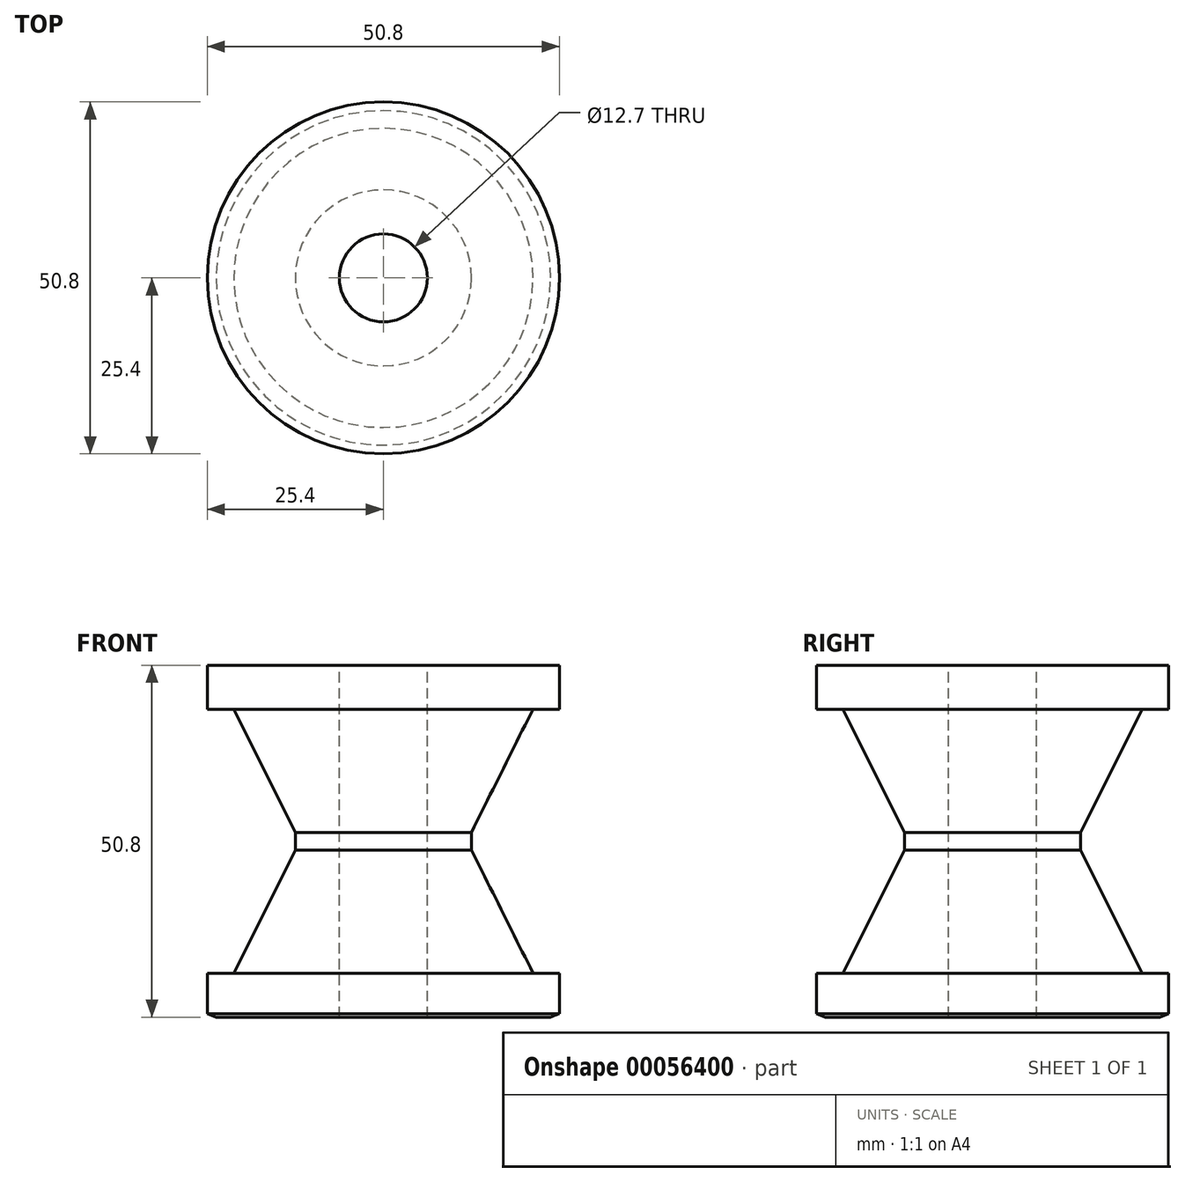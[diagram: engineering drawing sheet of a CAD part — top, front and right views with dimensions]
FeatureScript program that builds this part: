
annotation { "Feature Type Name" : "Feature", "Feature Type Description" : "" }
export const myFeature = defineFeature(function(context is Context, id is Id, definition is map)
    precondition{}
    {
        {
            var Q0;
            Q0=qCreatedBy(makeId("Front.planeOp"),FACE);
            var sketch = newSketch(context, id + "F0", { "sketchPlane" : qUnion([Q0])});
            skLineSegment(sketch, "E0.bottom", {"start": v(-12.7, 15.41) * mm, "end": v(-6.35, 15.41) * mm});
            skLineSegment(sketch, "E0.top", {"start": v(-12.7, -31.46) * mm, "end": v(-6.35, -31.46) * mm});
            skLineSegment(sketch, "E0.left", {"start": v(-12.7, 15.41) * mm, "end": v(-12.7, -31.46) * mm});
            skLineSegment(sketch, "E0.right", {"start": v(-6.35, 15.41) * mm, "end": v(-6.35, -31.46) * mm});
            skLineSegment(sketch, "E1.bottom", {"start": v(-6.35, 15.41) * mm, "end": v(-25.4, 15.41) * mm});
            skLineSegment(sketch, "E1.top", {"start": v(-6.35, 13) * mm, "end": v(-25.4, 13) * mm});
            skLineSegment(sketch, "E1.left", {"start": v(-6.35, 15.41) * mm, "end": v(-6.35, 13) * mm});
            skLineSegment(sketch, "E1.right", {"start": v(-25.4, 15.41) * mm, "end": v(-25.4, 13) * mm});
            skLineSegment(sketch, "E2.bottom", {"start": v(-6.35, -31.46) * mm, "end": v(-25.4, -31.46) * mm});
            skLineSegment(sketch, "E2.top", {"start": v(-6.35, -25.1) * mm, "end": v(-25.4, -25.1) * mm});
            skLineSegment(sketch, "E2.left", {"start": v(-6.35, -31.46) * mm, "end": v(-6.35, -25.1) * mm});
            skLineSegment(sketch, "E2.right", {"start": v(-25.4, -31.46) * mm, "end": v(-25.4, -25.1) * mm});
            skLineSegment(sketch, "E3.top", {"start": v(-6.35, 19.34) * mm, "end": v(-25.4, 19.34) * mm});
            skLineSegment(sketch, "E3.left", {"start": v(-6.35, 15.41) * mm, "end": v(-6.35, 19.34) * mm});
            skLineSegment(sketch, "E3.right", {"start": v(-25.4, 15.41) * mm, "end": v(-25.4, 19.34) * mm});
            skLineSegment(sketch, "E4", {"start": v(-31.56, 0) * mm, "end": v(32.14, 0) * mm, "construction": true});
            skLineSegment(sketch, "E5", {"start": v(0, 48.23) * mm, "end": v(0, -35.16) * mm, "construction": true});
            skSolve(sketch);
        }
        {
            var Q0;
            {var subQ5=sQuery(id+"F0.wireOp",EDGE,"E2.right");Q0=makeQuery(id+"F0.imprint","IMPRINT",FACE,{"disambiguationData":[TD([[makeQuery(id+"F0.imprint","IMPRINT",EDGE,{"derivedFrom":subQ5}),-1.0]])]});}
            var Q1;
            {var subQ5=sQuery(id+"F0.wireOp",EDGE,"E0.right");Q1=makeQuery(id+"F0.imprint","IMPRINT",FACE,{"disambiguationData":[TD([[makeQuery(id+"F0.imprint","IMPRINT",EDGE,{"derivedFrom":subQ5}),-1.0]])]});}
            var Q2;
            {var subQ5=sQuery(id+"F0.wireOp",EDGE,"E2.left");Q2=makeQuery(id+"F0.imprint","IMPRINT",FACE,{"disambiguationData":[TD([[makeQuery(id+"F0.imprint","IMPRINT",EDGE,{"derivedFrom":subQ5}),1.0]])]});}
            var Q3;
            {var subQ5=sQuery(id+"F0.wireOp",EDGE,"E1.left");Q3=makeQuery(id+"F0.imprint","IMPRINT",FACE,{"disambiguationData":[TD([[makeQuery(id+"F0.imprint","IMPRINT",EDGE,{"derivedFrom":subQ5}),-1.0]])]});}
            var Q4;
            {var subQ5=sQuery(id+"F0.wireOp",EDGE,"E1.right");Q4=makeQuery(id+"F0.imprint","IMPRINT",FACE,{"disambiguationData":[TD([[makeQuery(id+"F0.imprint","IMPRINT",EDGE,{"derivedFrom":subQ5}),1.0]])]});}
            var Q5;
            Q5=makeQuery(id+"F0.imprint","IMPRINT",FACE,{"disambiguationData":[TD([[makeQuery(id+"F0.imprint","IMPRINT",EDGE,{"derivedFrom":sQuery(id+"F0.wireOp",EDGE,"E3.top")}),1.0]])]});
            var Q6;
            Q6=sQuery(id+"F0.wireOp",EDGE,"E5");
            revolve(context, id + "F1", {"entities" : qUnion([Q0, Q1, Q2, Q3, Q4, Q5]), "axis" : qUnion([Q6]), "revolveType" : RevolveType.FULL});
        }
        {
            var Q0;
            Q0=makeQuery(id+"F1.opRevolve","SWEPT_EDGE",EDGE,{"disambiguationData":[OSD([sQuery(id+"F0.wireOp",EDGE,"E0.left"),sQuery(id+"F0.wireOp",EDGE,"E1.top")])]});
            var Q1;
            Q1=makeQuery(id+"F1.opRevolve","SWEPT_EDGE",EDGE,{"disambiguationData":[OSD([sQuery(id+"F0.wireOp",EDGE,"E0.left"),sQuery(id+"F0.wireOp",EDGE,"E2.top")])]});
            chamfer(context, id + "F2", {"entities" : qUnion([Q0, Q1]), "chamferType" : ChamferType.TWO_OFFSETS, "width1" : 8.9 * mm, "oppositeDirection" : false, "width2" : 17.78 * mm, "tangentPropagation" : true});
        }
        {
            var Q0;
            Q0=makeQuery(id+"F1.opRevolve","SWEPT_EDGE",EDGE,{"disambiguationData":[OSD([sQuery(id+"F0.wireOp",EDGE,"E2.bottom"),sQuery(id+"F0.wireOp",EDGE,"E2.right")])]});
            chamfer(context, id + "F3", {"entities" : qUnion([Q0]), "chamferType" : ChamferType.TWO_OFFSETS, "width1" : 0.5 * mm, "oppositeDirection" : false, "width2" : 1.27 * mm, "tangentPropagation" : true});
        }
        {
            var Q0;
            Q0=makeQuery(id+"F1.opRevolve","SWEPT_FACE",FACE,{"disambiguationData":[OSD([sQuery(id+"F0.wireOp",EDGE,"E2.bottom")])]});
            cPlane(context, id + "F4", {"entities" : qUnion([Q0]), "cplaneType" : CPlaneType.OFFSET, "offset" : 0 * mm, "width" : 152.4 * mm, "height" : 152.4 * mm});
        }
    });
